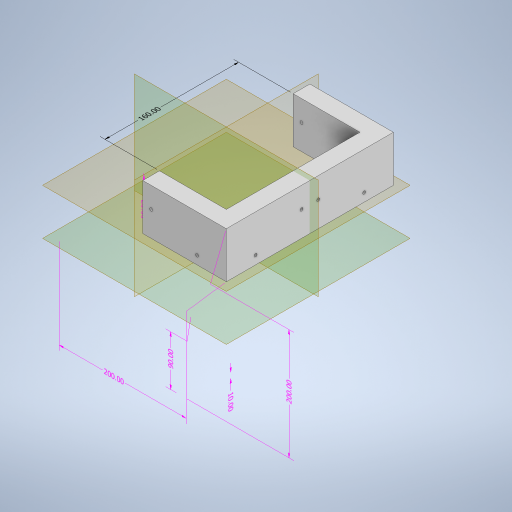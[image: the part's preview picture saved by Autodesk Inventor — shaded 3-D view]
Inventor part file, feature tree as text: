
AUTODESK INVENTOR PART (.ipt)
format: ipt  version: 2023 (Build 270158000, 158)  size: 436,224 bytes
history: native  units: mm
features: sketch x9, other x8, extrude x5, hole x4, plane x4, split x3
ambient origin geometry x8: Origin, YZ Plane, XZ Plane, XY Plane, X Axis, Y Axis, Z Axis, Center Point
bodies: Body1 (feature_tree)
feature tree (33):
  other  "Sólido1"
  other  "Anotaciones"
  extrude  "Extrusión1"  Depth=200.0mm
  hole  "Agujero1"  [1 undecoded]
  extrude  "Extrusión2"  Depth=15.0mm
  extrude  "Extrusión3"  Depth=80.0mm TaperAngle=0.0deg
  extrude  "Extrusión4"  Depth=200.0mm
  extrude  "Extrusión5"  Depth=20.0mm
  hole  "Agujero2"  [1 undecoded]
  plane  "Plano de trabajo1"
  split  "Dividir1"
  plane  "Plano de trabajo2"
  plane  "Plano de trabajo3"
  plane  "Plano de trabajo4"
  hole  "Agujero3"  [1 undecoded]
  hole  "Agujero4"  [1 undecoded]
  split  "Dividir2"
  split  "Dividir3"
  sketch  "Boceto2"  dims[d7=15.0mm d8=200.0mm]
  sketch  "Boceto3"  dims[d9=10.0mm d10=0.0mm]
  sketch  "Boceto4"  dims[d11=3.5mm d12=1.75mm d13=1.75mm d14=1.75mm d15=1.75mm d16=10.0mm d17=10.0mm d19=40.0mm]
  sketch  "Boceto5"  dims[d20=3.5mm d21=6.0mm d22=4.0mm d23=2.0mm d24=90.0deg d25=8.0mm d26=20.594885mm d27=15.0mm]
  sketch  "Boceto6"  dims[d28=20.0mm d29=80.0mm d30=0.0mm]
  sketch  "Boceto7"  dims[d31=57.0mm d32=200.0mm]
  sketch  "Boceto8"  dims[d33=110.0mm d34=0.0mm d36=20.0mm]
  sketch  "Boceto9"  dims[d37=20.0mm d38=20.0mm]
  sketch  "Boceto10"  dims[d39=90.0mm d40=0.0mm d43=30.0mm d44=0.0mm d45=3.5mm d46=1.75mm d47=1.75mm d48=1.75mm d49=1.75mm d50=10.0mm d51=10.0mm d52=15.0mm d53=10.0mm d54=10.0mm d55=15.0mm d56=3.5mm d57=6.0mm d58=4.0mm d59=2.0mm d60=90.0deg d61=8.0mm d62=20.594885mm d63=10.0mm d65=10.0mm d75=200.0mm d76=10.0mm d77=20.0mm d81=40.0mm d88=90.0deg d89=10.0mm d90=30.0mm d91=5.0mm d92=5.0mm d93=5.0mm d94=5.0mm d95=30.0mm d96=5.0mm d97=5.0mm d98=3.5mm d99=5.0mm d100=5.0mm d101=5.0mm d102=5.0mm d103=5.0mm d104=20.0mm d105=3.5mm d106=6.0mm d107=4.0mm d108=2.0mm d109=90.0deg d110=8.0mm d111=20.594885mm d112=10.0mm d113=30.0mm d114=5.0mm d115=5.0mm d116=5.0mm d117=5.0mm d118=5.0mm d119=5.0mm d120=3.5mm d121=5.0mm d122=5.0mm d123=5.0mm d124=5.0mm d125=5.0mm d126=30.0mm d127=30.0mm d128=3.5mm d129=6.0mm d130=4.0mm d131=2.0mm d132=90.0deg d133=8.0mm d134=20.594885mm d66=5.760865mm d67=7.72461mm d68=200.0mm d69=3.008686mm d70=2.422102mm d71=10.0mm d72=3.500509mm d73=2.402572mm d74=90.0mm d78=3.13122mm d79=6.269346mm d80=200.0mm d82=8.450127mm d83=0.968417mm d84=20.0mm d85=4.759975mm d86=4.646891mm d87=160.0mm]
  other  "Cota lineal 1"
  other  "Cota lineal 2"
  other  "Cota lineal 3"
  other  "Cota lineal 4"
  other  "Cota lineal 5"
  other  "Cota lineal 6"
note: 4 required parameter values undecoded (feature->parameter linkage not recoverable at this tier; creation-order binding heuristic only, values carry confidence <= 0.55)
